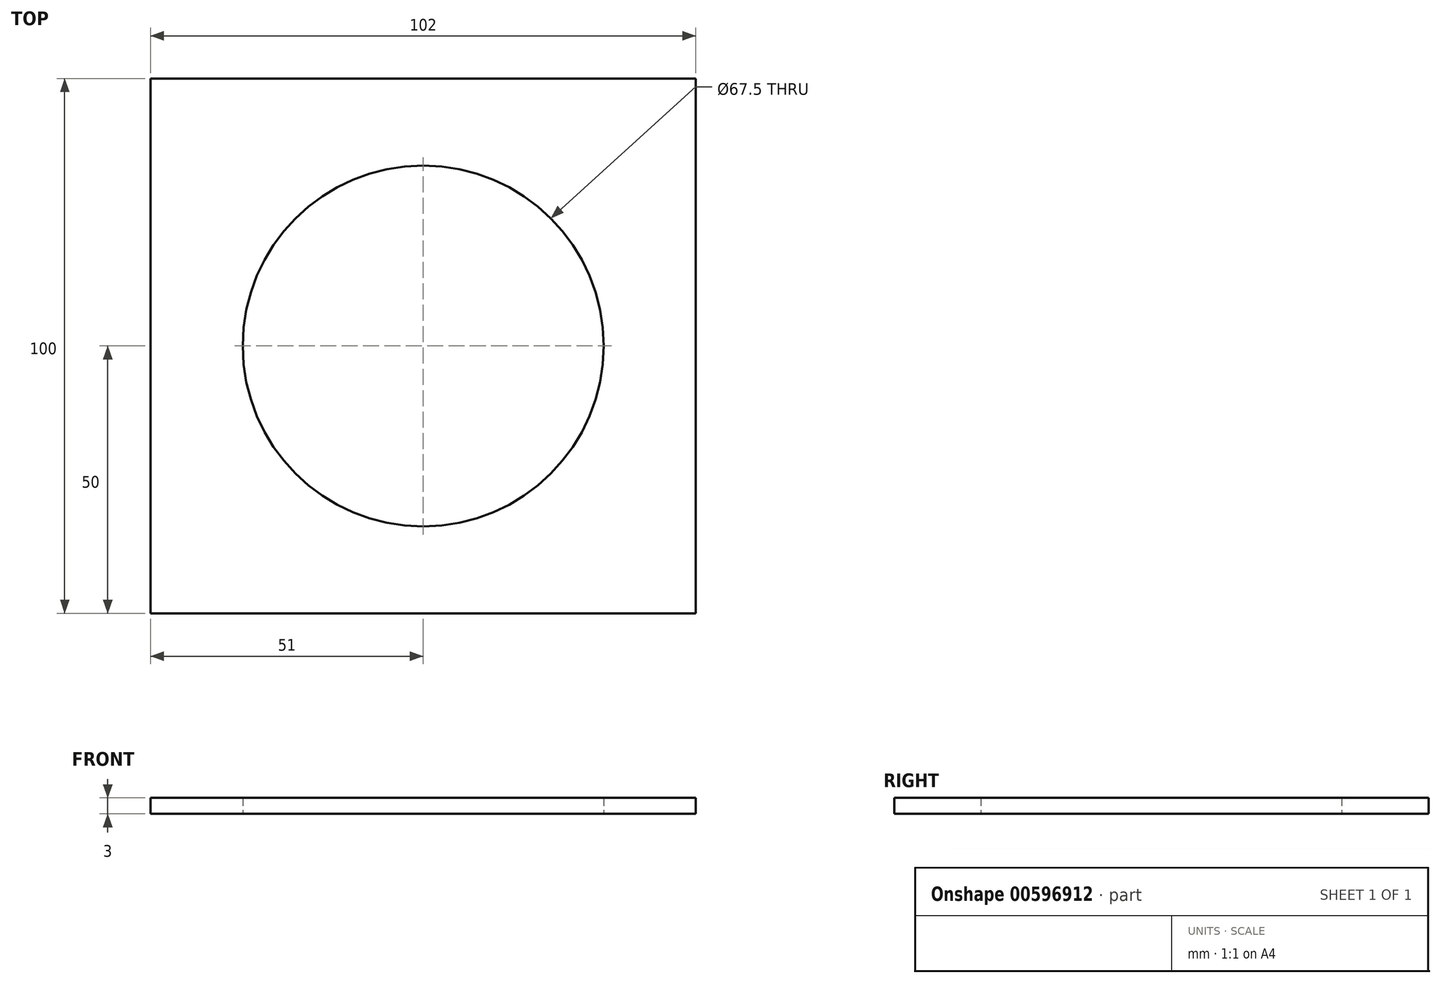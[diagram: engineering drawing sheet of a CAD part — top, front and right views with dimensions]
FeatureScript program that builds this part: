
annotation { "Feature Type Name" : "Feature", "Feature Type Description" : "" }
export const myFeature = defineFeature(function(context is Context, id is Id, definition is map)
    precondition{}
    {
        {
            var Q0;
            Q0=qCreatedBy(makeId("Top.planeOp"),FACE);
            var sketch = newSketch(context, id + "F0", { "sketchPlane" : qUnion([Q0])});
            skCircle(sketch, "E0", {"center": v(0, 0) * mm, "radius": 33.75 * mm});
            skLineSegment(sketch, "E1.bottom", {"start": v(51, 50) * mm, "end": v(-51, 50) * mm});
            skLineSegment(sketch, "E1.top", {"start": v(51, -50) * mm, "end": v(-51, -50) * mm});
            skLineSegment(sketch, "E1.left", {"start": v(51, 50) * mm, "end": v(51, -50) * mm});
            skLineSegment(sketch, "E1.right", {"start": v(-51, 50) * mm, "end": v(-51, -50) * mm});
            skSolve(sketch);
        }
        {
            var Q0;
            Q0=makeQuery(id+"F0.imprint","IMPRINT",FACE,{"disambiguationData":[TD([[makeQuery(id+"F0.imprint","IMPRINT",EDGE,{"derivedFrom":sQuery(id+"F0.wireOp",EDGE,"E0")}),-1.0]])]});
            extrude(context, id + "F1", {"entities" : qUnion([Q0]), "depth" : 3 * mm, "offsetDistance" : 25 * mm});
        }
    });
